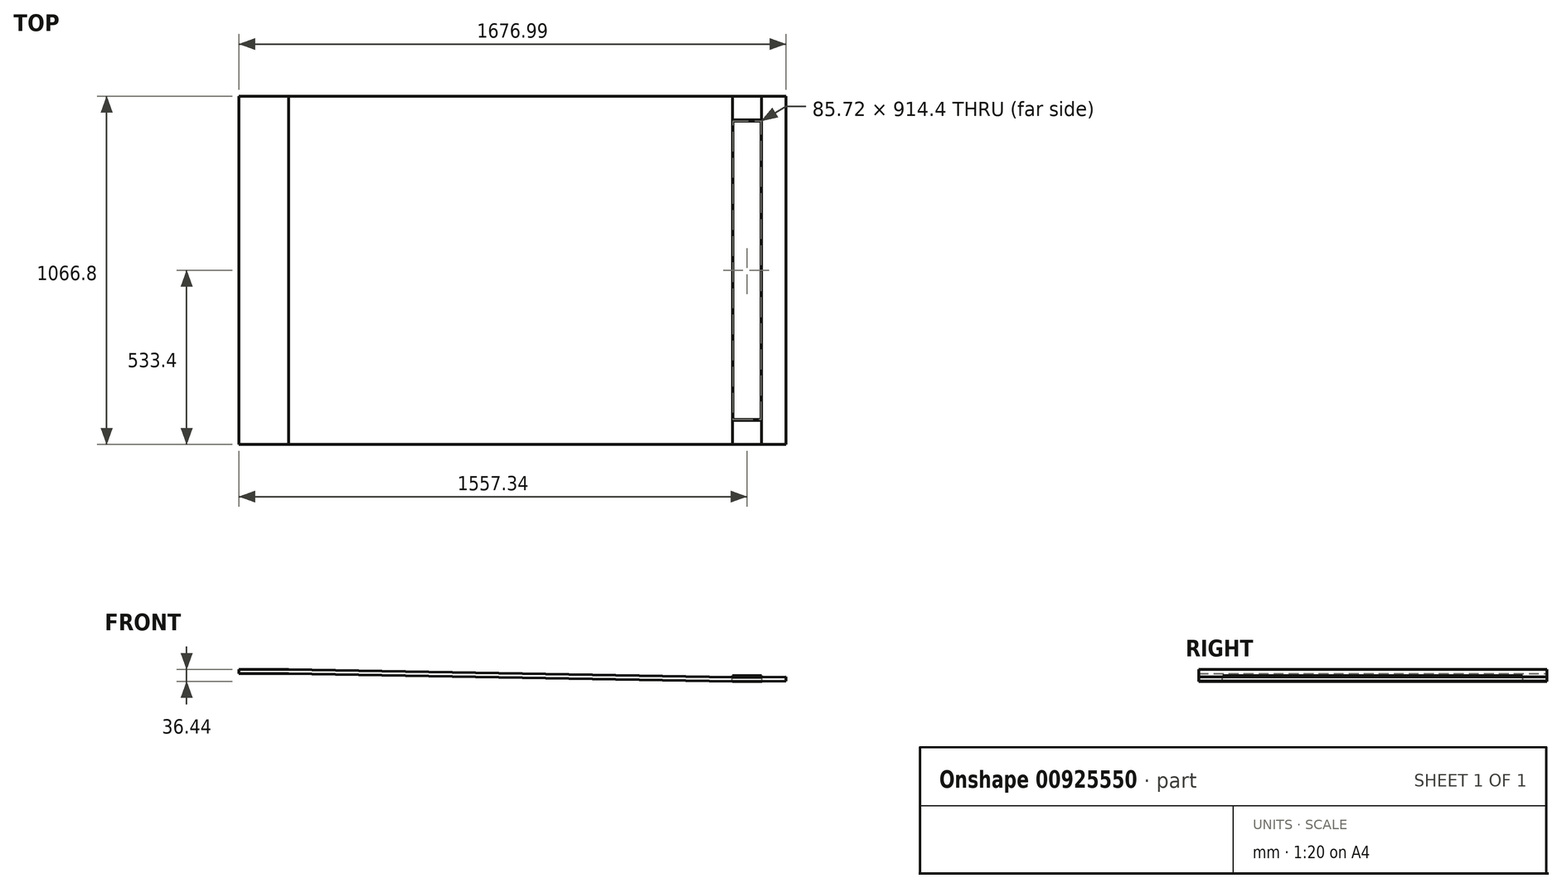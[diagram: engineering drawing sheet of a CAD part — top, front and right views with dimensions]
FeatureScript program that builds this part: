
annotation { "Feature Type Name" : "Feature", "Feature Type Description" : "" }
export const myFeature = defineFeature(function(context is Context, id is Id, definition is map)
    precondition{}
    {
        {
            var Q0;
            Q0=qCreatedBy(makeId("Top.planeOp"),FACE);
            var sketch = newSketch(context, id + "F0", { "sketchPlane" : qUnion([Q0])});
            skCircle(sketch, "E0", {"center": v(0, 0) * mm, "radius": 25.4 * mm});
            skLineSegment(sketch, "E1.bottom", {"start": v(42.86, -457.2) * mm, "end": v(-42.86, -457.2) * mm});
            skLineSegment(sketch, "E1.top", {"start": v(42.86, 457.2) * mm, "end": v(-42.86, 457.2) * mm});
            skLineSegment(sketch, "E1.left", {"start": v(42.86, -457.2) * mm, "end": v(42.86, 457.2) * mm});
            skLineSegment(sketch, "E1.right", {"start": v(-42.86, -457.2) * mm, "end": v(-42.86, 457.2) * mm});
            skCircle(sketch, "E2", {"center": v(0, 0) * mm, "radius": 22.23 * mm});
            skSolve(sketch);
        }
        {
            var Q0;
            Q0=makeQuery(id+"F0.imprint","IMPRINT",FACE,{"disambiguationData":[TD([[makeQuery(id+"F0.imprint","IMPRINT",EDGE,{"derivedFrom":sQuery(id+"F0.wireOp",EDGE,"E0")}),-1.0]])]});
            var Q1;
            Q1=makeQuery(id+"F0.imprint","IMPRINT",FACE,{"disambiguationData":[TD([[makeQuery(id+"F0.imprint","IMPRINT",EDGE,{"derivedFrom":sQuery(id+"F0.wireOp",EDGE,"E0")}),1.0]])]});
            var Q2;
            Q2=makeQuery(id+"F0.imprint","IMPRINT",FACE,{"disambiguationData":[TD([[makeQuery(id+"F0.imprint","IMPRINT",EDGE,{"derivedFrom":sQuery(id+"F0.wireOp",EDGE,"E1.bottom")}),-1.0]])]});
            var Q3;
            Q3=makeQuery(id+"F0.imprint","IMPRINT",FACE,{"disambiguationData":[TD([[makeQuery(id+"F0.imprint","IMPRINT",EDGE,{"derivedFrom":sQuery(id+"F0.wireOp",EDGE,"E2")}),1.0]])]});
            extrude(context, id + "F1", {"entities" : qUnion([Q0, Q1, Q2, Q3]), "oppositeDirection" : true, "depth" : 38.1 * mm, "offsetDistance" : 30.48 * mm});
        }
        {
            var Q0;
            Q0=makeQuery(id+"F0.imprint","IMPRINT",FACE,{"disambiguationData":[TD([[makeQuery(id+"F0.imprint","IMPRINT",EDGE,{"derivedFrom":sQuery(id+"F0.wireOp",EDGE,"E2")}),1.0]])]});
            var Q1;
            Q1=sQuery(id+"F0.wireOp",EDGE,"E0");
            extrude(context, id + "F2", {"entities" : qUnion([Q0]), "operationType" : NewBodyOperationType.ADD, "surfaceEntities" : qUnion([Q1]), "oppositeDirection" : true, "depth" : 76.2 * mm, "offsetDistance" : 30.48 * mm});
        }
        {
            var Q0;
            Q0=makeQuery(id+"F1.opExtrude","SWEPT_FACE",FACE,{"disambiguationData":[OSD([sQuery(id+"F0.wireOp",EDGE,"E1.left")])]});
            var sketch = newSketch(context, id + "F3", { "sketchPlane" : qUnion([Q0])});
            skLineSegment(sketch, "E3", {"start": v(0, -38.1) * mm, "end": v(-457.2, -19.05) * mm});
            skLineSegment(sketch, "E4", {"start": v(-457.2, -19.05) * mm, "end": v(-457.2, -38.1) * mm});
            skLineSegment(sketch, "E5", {"start": v(-457.2, -38.1) * mm, "end": v(0, -38.1) * mm});
            skPoint(sketch, "E6", {"position": v(-457.2, 0) * mm});
            skLineSegment(sketch, "E7", {"start": v(0, -38.1) * mm, "end": v(0, 69.3) * mm, "construction": true});
            skLineSegment(sketch, "E8.MirrorCS", {"start": v(457.2, -19.05) * mm, "end": v(457.2, -38.1) * mm});
            skLineSegment(sketch, "E9.MirrorCS", {"start": v(0, -38.1) * mm, "end": v(457.2, -19.05) * mm});
            skLineSegment(sketch, "E10.MirrorCS", {"start": v(457.2, -38.1) * mm, "end": v(0, -38.1) * mm});
            skSolve(sketch);
        }
        {
            var Q0;
            Q0 = qSketchRegion(id + "F3", true);
            extrude(context, id + "F4", {"entities" : qUnion([Q0]), "operationType" : NewBodyOperationType.REMOVE, "endBound" : BoundingType.THROUGH_ALL, "oppositeDirection" : true, "depth" : 30.48 * mm, "offsetDistance" : 30.48 * mm});
        }
        {
            var Q0;
            Q0=makeQuery(id+"F1.opExtrude","CAP_FACE",FACE,{"disambiguationData":[OSD([sQuery(id+"F0.wireOp",EDGE,"E1.bottom"),sQuery(id+"F0.wireOp",EDGE,"E1.top"),sQuery(id+"F0.wireOp",EDGE,"E1.left"),sQuery(id+"F0.wireOp",EDGE,"E1.right")])],"isStart":true});
            var sketch = newSketch(context, id + "F5", { "sketchPlane" : qUnion([Q0])});
            skLineSegment(sketch, "E11.0", {"start": v(42.86, -457.2) * mm, "end": v(42.86, 457.2) * mm});
            skLineSegment(sketch, "E11.1", {"start": v(42.86, -457.2) * mm, "end": v(-42.86, -457.2) * mm});
            skLineSegment(sketch, "E11.2", {"start": v(-42.86, -457.2) * mm, "end": v(-42.86, 457.2) * mm});
            skLineSegment(sketch, "E11.3", {"start": v(42.86, 457.2) * mm, "end": v(-42.86, 457.2) * mm});
            skLineSegment(sketch, "E12.0", {"start": v(-44.45, -458.79) * mm, "end": v(-44.45, 458.79) * mm});
            skLineSegment(sketch, "E12.1", {"start": v(44.45, -458.79) * mm, "end": v(-44.45, -458.79) * mm});
            skLineSegment(sketch, "E12.2", {"start": v(44.45, -458.79) * mm, "end": v(44.45, 458.79) * mm});
            skLineSegment(sketch, "E12.3", {"start": v(44.45, 458.79) * mm, "end": v(-44.45, 458.79) * mm});
            skSolve(sketch);
        }
        {
            var Q0;
            Q0=makeQuery(id+"F5.imprint","IMPRINT",FACE,{"disambiguationData":[TD([[makeQuery(id+"F5.imprint","IMPRINT",EDGE,{"derivedFrom":sQuery(id+"F5.wireOp",EDGE,"E11.0")}),-1.0]])]});
            var Q1;
            Q1 = qConstructionFilter(qBodyType(qCreatedBy(id + "F5" ,EDGE), BodyType.WIRE), ConstructionObject.NO);
            extrude(context, id + "F6", {"entities" : qUnion([Q0]), "surfaceEntities" : qUnion([Q1]), "oppositeDirection" : true, "depth" : 6.35 * mm, "offsetDistance" : 30.48 * mm});
        }
        {
            var Q0;
            Q0=qCreatedBy(makeId("Top.planeOp"),FACE);
            cPlane(context, id + "F7", {"entities" : qUnion([Q0]), "cplaneType" : CPlaneType.OFFSET, "offset" : 0.12 / 50.8 * mm, "width" : 152.4 * mm, "height" : 152.4 * mm});
        }
        {
            var Q0;
            Q0=qCreatedBy(id+"F7.planeOp",FACE);
            var sketch = newSketch(context, id + "F8", { "sketchPlane" : qUnion([Q0])});
            skLineSegment(sketch, "E13.bottom", {"start": v(-1404.94, 533.4) * mm, "end": v(119.06, 533.4) * mm, "construction": true});
            skLineSegment(sketch, "E13.top", {"start": v(-1404.94, -533.4) * mm, "end": v(119.06, -533.4) * mm, "construction": true});
            skLineSegment(sketch, "E13.left", {"start": v(-1404.94, 533.4) * mm, "end": v(-1404.94, -533.4) * mm, "construction": true});
            skLineSegment(sketch, "E13.right", {"start": v(119.06, 533.4) * mm, "end": v(119.06, -533.4) * mm, "construction": true});
            skLineSegment(sketch, "E14.0.0", {"start": v(42.86, -457.2) * mm, "end": v(42.86, 457.2) * mm, "construction": true});
            skLineSegment(sketch, "E14.0.1", {"start": v(42.86, 457.2) * mm, "end": v(-42.86, 457.2) * mm, "construction": true});
            skLineSegment(sketch, "E14.0.2", {"start": v(-42.86, 457.2) * mm, "end": v(-42.86, -457.2) * mm, "construction": true});
            skLineSegment(sketch, "E14.0.3", {"start": v(-42.86, -457.2) * mm, "end": v(42.86, -457.2) * mm, "construction": true});
            skLineSegment(sketch, "E15", {"start": v(119.06, 0) * mm, "end": v(-1404.94, 0) * mm, "construction": true});
            skPoint(sketch, "E16", {"position": v(-44.45, 0) * mm});
            skPoint(sketch, "E17", {"position": v(44.45, 0) * mm});
            skLineSegment(sketch, "E18.0", {"start": v(-44.45, -458.79) * mm, "end": v(-44.45, 458.79) * mm, "construction": true});
            skLineSegment(sketch, "E19.0", {"start": v(44.45, -458.79) * mm, "end": v(44.45, 458.79) * mm, "construction": true});
            skSolve(sketch);
        }
        {
            var Q0;
            Q0=qCreatedBy(makeId("Front.planeOp"),FACE);
            var sketch = newSketch(context, id + "F9", { "sketchPlane" : qUnion([Q0])});
            skLineSegment(sketch, "E20.0", {"start": v(119.06, 1.59) * mm, "end": v(-1404.94, 1.59) * mm, "construction": true});
            skPoint(sketch, "E20.1", {"position": v(-44.45, 1.59) * mm});
            skLineSegment(sketch, "E21", {"start": v(-44.45, 1.59) * mm, "end": v(-1404.94, 25.33) * mm, "construction": true});
            skPoint(sketch, "E22.0", {"position": v(44.45, 1.59) * mm});
            skLineSegment(sketch, "E23", {"start": v(44.45, 1.59) * mm, "end": v(119.06, 2.89) * mm, "construction": true});
            skLineSegment(sketch, "E24.0", {"start": v(-44.56, -4.76) * mm, "end": v(-1404.94, 18.98) * mm});
            skLineSegment(sketch, "E25.0", {"start": v(44.56, -4.76) * mm, "end": v(119.2, -3.46) * mm});
            skLineSegment(sketch, "E26.0", {"start": v(45, -17.46) * mm, "end": v(119.65, -16.15) * mm});
            skLineSegment(sketch, "E27", {"start": v(44.56, -4.76) * mm, "end": v(45, -17.46) * mm});
            skLineSegment(sketch, "E28", {"start": v(119.2, -3.46) * mm, "end": v(119.65, -16.15) * mm});
            skLineSegment(sketch, "E29.0", {"start": v(-44.78, -17.46) * mm, "end": v(-1405.16, 6.29) * mm});
            skLineSegment(sketch, "E30", {"start": v(-44.78, -17.46) * mm, "end": v(-44.56, -4.76) * mm});
            skLineSegment(sketch, "E31", {"start": v(-44.56, -4.76) * mm, "end": v(44.56, -4.76) * mm});
            skLineSegment(sketch, "E32", {"start": v(-44.78, -17.46) * mm, "end": v(45, -17.46) * mm});
            skLineSegment(sketch, "E33.bottom", {"start": v(-1404.94, 18.98) * mm, "end": v(-1557.34, 18.98) * mm});
            skLineSegment(sketch, "E33.top", {"start": v(-1404.94, 6.29) * mm, "end": v(-1557.34, 6.29) * mm});
            skLineSegment(sketch, "E33.left", {"start": v(-1404.94, 18.98) * mm, "end": v(-1404.94, 6.29) * mm});
            skLineSegment(sketch, "E33.right", {"start": v(-1557.34, 18.98) * mm, "end": v(-1557.34, 6.29) * mm});
            skLineSegment(sketch, "E34", {"start": v(-1405.16, 6.29) * mm, "end": v(-1404.94, 6.29) * mm});
            skSolve(sketch);
        }
        {
            var Q0;
            Q0=makeQuery(id+"F9.imprint","IMPRINT",FACE,{"disambiguationData":[TD([[makeQuery(id+"F9.imprint","IMPRINT",EDGE,{"derivedFrom":sQuery(id+"F9.wireOp",EDGE,"E25.0")}),-1.0]])]});
            var Q1;
            Q1=makeQuery(id+"F9.imprint","IMPRINT",FACE,{"disambiguationData":[TD([[makeQuery(id+"F9.imprint","IMPRINT",EDGE,{"derivedFrom":sQuery(id+"F9.wireOp",EDGE,"E24.0")}),1.0]])]});
            var Q2;
            Q2=makeQuery(id+"F9.imprint","IMPRINT",FACE,{"disambiguationData":[TD([[makeQuery(id+"F9.imprint","IMPRINT",EDGE,{"derivedFrom":sQuery(id+"F9.wireOp",EDGE,"E33.bottom")}),1.0]])]});
            var Q3;
            Q3=makeQuery(id+"F9.imprint","IMPRINT",FACE,{"disambiguationData":[TD([[makeQuery(id+"F9.imprint","IMPRINT",EDGE,{"derivedFrom":sQuery(id+"F9.wireOp",EDGE,"E27")}),-1.0]])]});
            var Q4;
            Q4=sQuery(id+"F8.wireOp",VERTEX,"E13.top.end");
            var Q5;
            Q5=sQuery(id+"F8.wireOp",VERTEX,"E13.bottom.start");
            extrude(context, id + "F10", {"entities" : qUnion([Q0, Q1, Q2, Q3]), "endBound" : BoundingType.UP_TO_VERTEX, "depth" : 30.48 * mm, "endBoundEntityVertex" : qUnion([Q4]), "offsetDistance" : 30.48 * mm, "hasSecondDirection" : true, "secondDirectionBound" : SecondDirectionBoundingType.UP_TO_VERTEX, "secondDirectionOppositeDirection" : true, "secondDirectionDepth" : 30.48 * mm, "secondDirectionBoundEntityVertex" : qUnion([Q5])});
        }
        {
            var Q0;
            Q0=makeQuery(id+"F10.opExtrude","SWEPT_FACE",FACE,{"disambiguationData":[OSD([sQuery(id+"F9.wireOp",EDGE,"E31")])]});
            var sketch = newSketch(context, id + "F11", { "sketchPlane" : qUnion([Q0])});
            skLineSegment(sketch, "E35.0", {"start": v(44.45, 458.79) * mm, "end": v(-44.45, 458.79) * mm, "construction": true});
            skLineSegment(sketch, "E35.1", {"start": v(-44.45, -458.79) * mm, "end": v(-44.45, 458.79) * mm, "construction": true});
            skLineSegment(sketch, "E35.2", {"start": v(44.45, -458.79) * mm, "end": v(44.45, 458.79) * mm, "construction": true});
            skLineSegment(sketch, "E35.3", {"start": v(44.45, -458.79) * mm, "end": v(-44.45, -458.79) * mm, "construction": true});
            skLineSegment(sketch, "E36.0", {"start": v(-46.04, -460.38) * mm, "end": v(-46.04, 460.38) * mm});
            skLineSegment(sketch, "E36.1", {"start": v(46.04, -460.38) * mm, "end": v(-46.04, -460.38) * mm});
            skLineSegment(sketch, "E36.2", {"start": v(46.04, -460.38) * mm, "end": v(46.04, 460.38) * mm});
            skLineSegment(sketch, "E36.3", {"start": v(46.04, 460.38) * mm, "end": v(-46.04, 460.38) * mm});
            skSolve(sketch);
        }
        {
            var Q0;
            {var subQ0=sQuery(id+"F11.wireOp",EDGE,"E36.1");var subQ1=makeQuery(id+"F9.imprint","IMPRINT",EDGE,{"derivedFrom":sQuery(id+"F9.wireOp",EDGE,"E31")});var subQ2=makeQuery(id+"F10.opExtrude","TWEAK_EDGE",EDGE,{"derivedFrom":[makeQuery(id+"F9.imprint","IMPRINT",EDGE,{"derivedFrom":sQuery(id+"F9.wireOp",EDGE,"E25.0")}),subQ1]});var subQ3=makeQuery(id+"F11.imprint","INTERSECT",VERTEX,{"derivedFrom":[subQ2,subQ0]});Q0=makeQuery(id+"F11.imprint","IMPRINT",FACE,{"disambiguationData":[TD([[makeQuery(id+"F11.imprint","IMPRINT",EDGE,{"disambiguationData":[TD([[subQ3,-1.0]])],"derivedFrom":subQ0}),-1.0]])]});}
            extrude(context, id + "F12", {"entities" : qUnion([Q0]), "operationType" : NewBodyOperationType.REMOVE, "endBound" : BoundingType.THROUGH_ALL, "oppositeDirection" : true, "depth" : 30.48 * mm, "offsetDistance" : 30.48 * mm});
        }
    });
